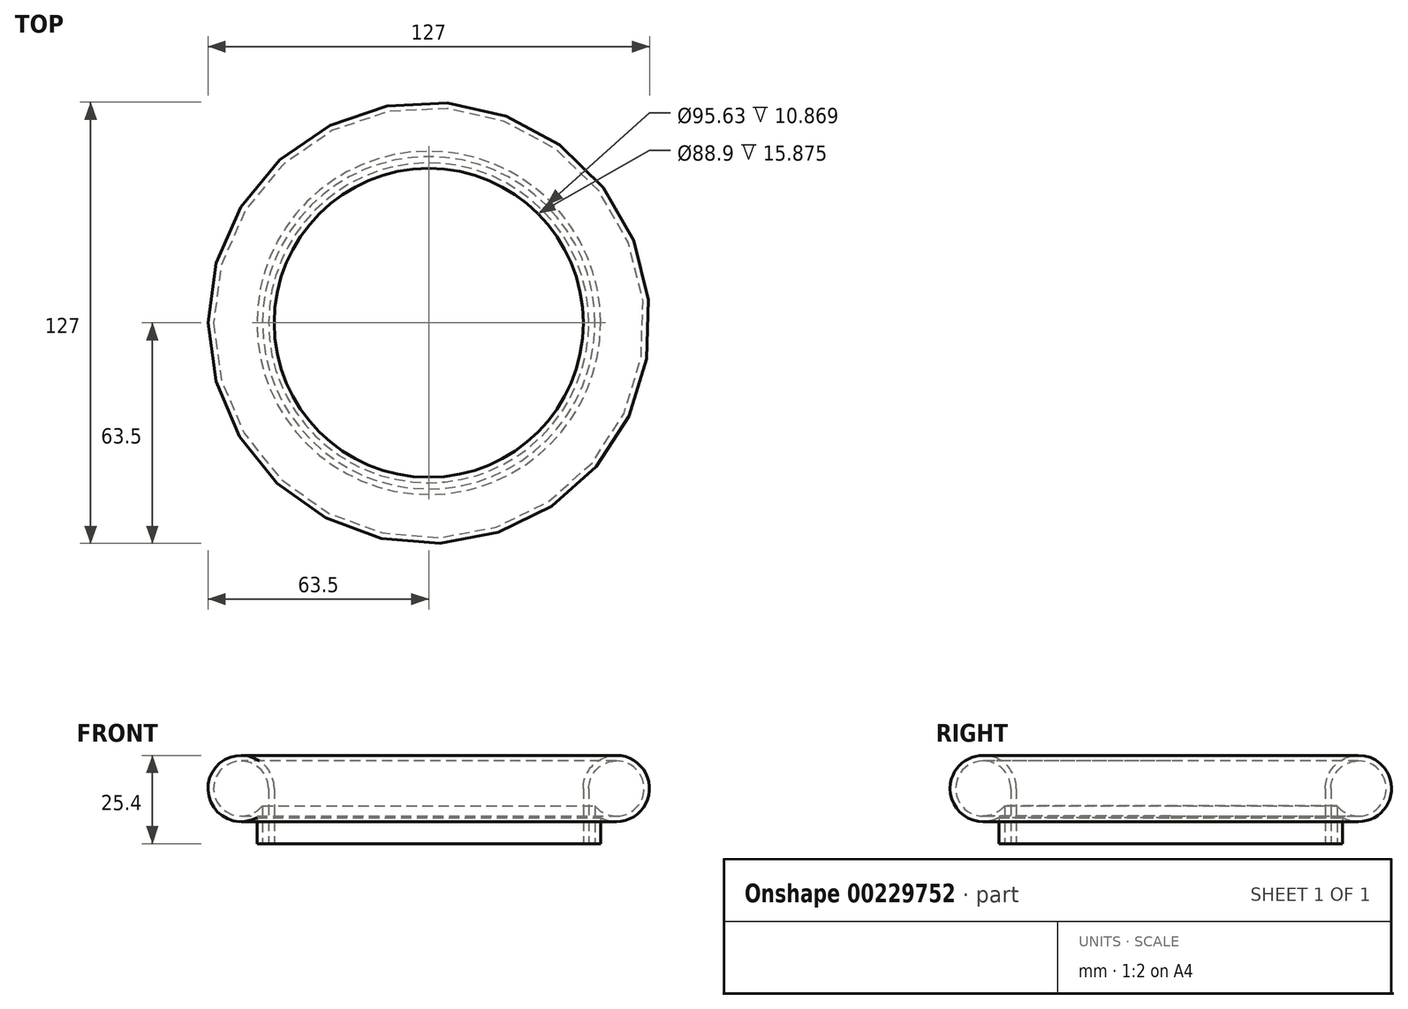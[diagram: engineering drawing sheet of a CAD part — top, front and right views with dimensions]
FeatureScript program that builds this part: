
annotation { "Feature Type Name" : "Feature", "Feature Type Description" : "" }
export const myFeature = defineFeature(function(context is Context, id is Id, definition is map)
    precondition{}
    {
        {
            var Q0;
            Q0=qCreatedBy(makeId("Front.planeOp"),FACE);
            var sketch = newSketch(context, id + "F0", { "sketchPlane" : qUnion([Q0])});
            skArc(sketch, "E0", {"start": v(47.82, 10.87) * mm, "mid": v(61.45, 18.53) * mm, "end": v(46.04, 15.88) * mm});
            skArc(sketch, "E1", {"start": v(49.42, 7.51) * mm, "mid": v(62.17, 20.74) * mm, "end": v(44.45, 15.88) * mm});
            skLineSegment(sketch, "E2", {"start": v(46.04, 15.88) * mm, "end": v(46.04, 0) * mm});
            skLineSegment(sketch, "E3", {"start": v(46.04, 0) * mm, "end": v(44.45, 0) * mm});
            skLineSegment(sketch, "E4", {"start": v(44.45, 0) * mm, "end": v(44.45, 15.88) * mm});
            skLineSegment(sketch, "E5", {"start": v(47.82, 10.87) * mm, "end": v(47.82, 0) * mm});
            skLineSegment(sketch, "E6", {"start": v(47.82, 0) * mm, "end": v(49.42, 0) * mm});
            skLineSegment(sketch, "E7", {"start": v(49.42, 0) * mm, "end": v(49.42, 7.51) * mm});
            skLineSegment(sketch, "E8", {"start": v(0, 0) * mm, "end": v(0, 38.59) * mm, "construction": true});
            skSolve(sketch);
        }
        {
            var Q0;
            Q0=makeQuery(id+"F0.imprint","IMPRINT",FACE,{"disambiguationData":[TD([[makeQuery(id+"F0.imprint","IMPRINT",EDGE,{"derivedFrom":sQuery(id+"F0.wireOp",EDGE,"E0")}),-1.0]])]});
            var Q1;
            Q1=sQuery(id+"F0.wireOp",EDGE,"E8");
            revolve(context, id + "F1", {"entities" : qUnion([Q0]), "axis" : qUnion([Q1]), "revolveType" : RevolveType.FULL});
        }
    });
